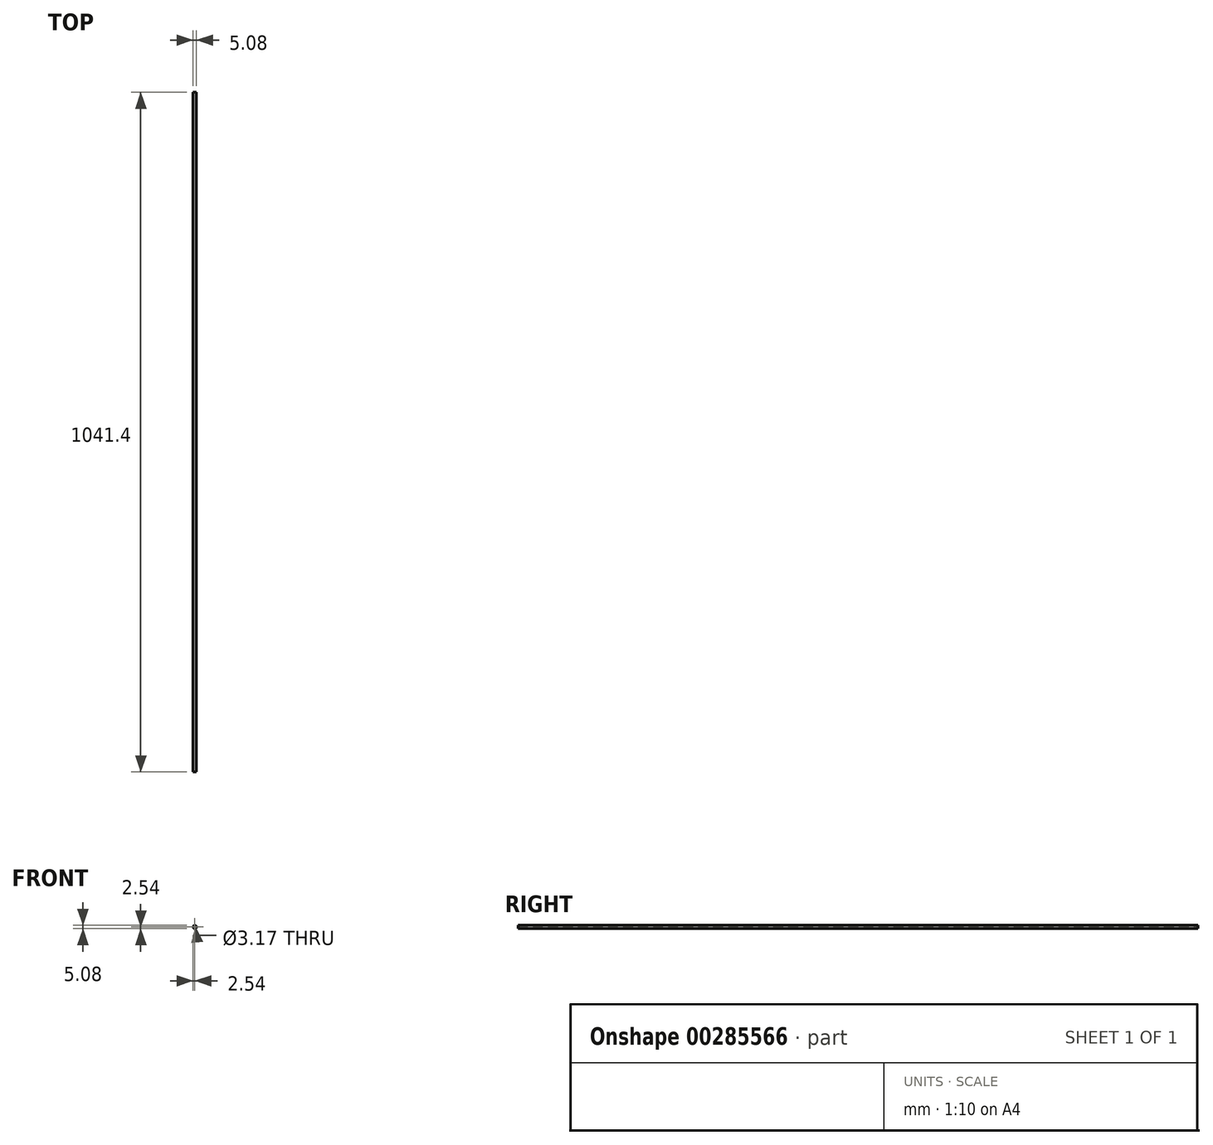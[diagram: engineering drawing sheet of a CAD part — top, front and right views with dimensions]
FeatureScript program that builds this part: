
annotation { "Feature Type Name" : "Feature", "Feature Type Description" : "" }
export const myFeature = defineFeature(function(context is Context, id is Id, definition is map)
    precondition{}
    {
        {
            var Q0;
            Q0=qCreatedBy(makeId("Front.planeOp"),FACE);
            var sketch = newSketch(context, id + "F0", { "sketchPlane" : qUnion([Q0])});
            skCircle(sketch, "E0", {"center": v(0, 0) * mm, "radius": 2.54 * mm});
            skCircle(sketch, "E1", {"center": v(0, 0) * mm, "radius": 1.59 * mm});
            skSolve(sketch);
        }
        {
            var Q0;
            Q0=makeQuery(id+"F0.imprint","IMPRINT",FACE,{"disambiguationData":[TD([[makeQuery(id+"F0.imprint","IMPRINT",EDGE,{"derivedFrom":sQuery(id+"F0.wireOp",EDGE,"E0")}),1.0]])]});
            extrude(context, id + "F1", {"entities" : qUnion([Q0]), "depth" : 1041.4 * mm});
        }
    });
